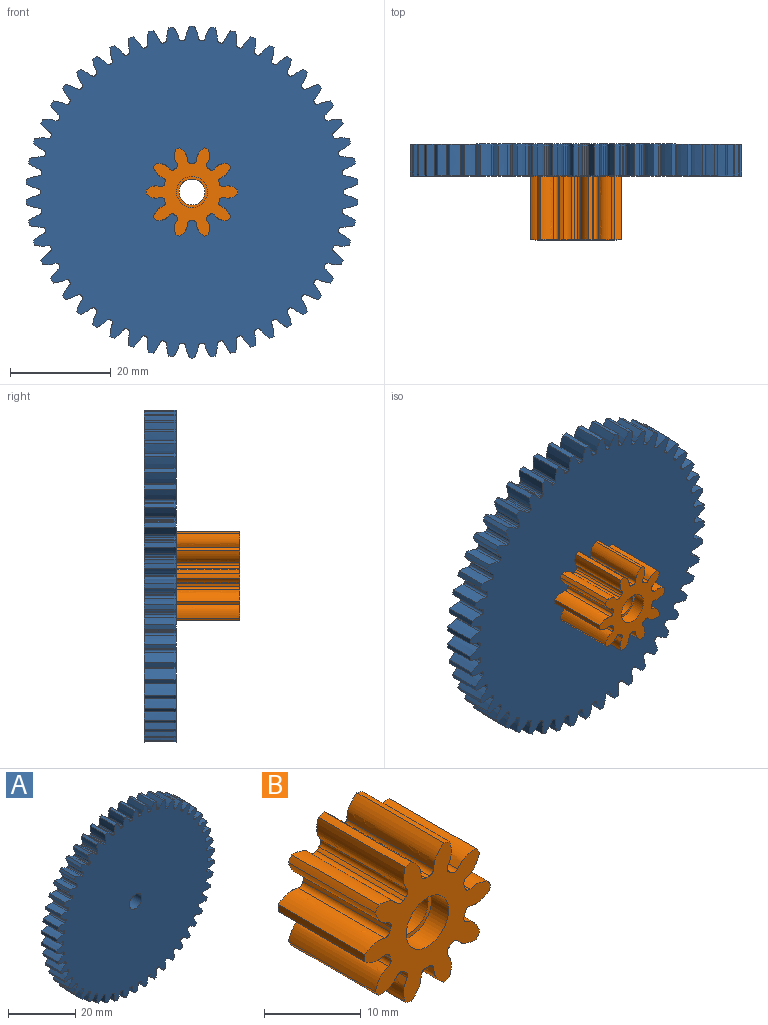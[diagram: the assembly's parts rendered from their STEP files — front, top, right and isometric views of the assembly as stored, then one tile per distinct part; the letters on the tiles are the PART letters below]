
ASSEMBLY  parts=2 mates=1
PART A: 305 faces, bbox 66x6.4x66 mm
  f0: cylinder r=2.59mm len=5.18mm, axis (0,-1,0), area 62.7mm2, adj f50,f303
  f1: cylinder r=33.02mm len=6.35mm, axis (0,1,0), area 6.2mm2, adj f50,f52,f53,f300
  f2: cylinder r=33.02mm len=6.35mm, axis (0,1,0), area 6.2mm2, adj f50,f52,f295,f298
  f3: cylinder r=33.02mm len=6.35mm, axis (0,1,0), area 6.2mm2, adj f50,f52,f290,f293
  f4: cylinder r=33.02mm len=6.35mm, axis (0,1,0), area 6.2mm2, adj f50,f52,f285,f288
  f5: cylinder r=33.02mm len=6.35mm, axis (0,1,0), area 6.2mm2, adj f50,f52,f263,f280
  f6: cylinder r=33.02mm len=6.35mm, axis (0,1,0), area 6.2mm2, adj f50,f52,f275,f278
  f7: cylinder r=33.02mm len=6.35mm, axis (0,1,0), area 6.2mm2, adj f50,f52,f270,f283
  f8: cylinder r=33.02mm len=6.35mm, axis (0,1,0), area 6.2mm2, adj f50,f52,f265,f268
  f9: cylinder r=33.02mm len=6.35mm, axis (0,1,0), area 6.2mm2, adj f50,f52,f260,f273
  f10: cylinder r=33.02mm len=6.35mm, axis (0,1,0), area 6.2mm2, adj f50,f52,f255,f258
  f11: cylinder r=33.02mm len=6.35mm, axis (0,1,0), area 6.2mm2, adj f50,f52,f250,f253
  f12: cylinder r=33.02mm len=6.35mm, axis (0,1,0), area 6.2mm2, adj f50,f52,f245,f248
  f13: cylinder r=33.02mm len=6.35mm, axis (0,1,0), area 6.2mm2, adj f50,f52,f240,f243
  f14: cylinder r=33.02mm len=6.35mm, axis (0,1,0), area 6.2mm2, adj f50,f52,f235,f238
  f15: cylinder r=33.02mm len=6.35mm, axis (0,1,0), area 6.2mm2, adj f50,f52,f230,f233
  f16: cylinder r=33.02mm len=6.35mm, axis (0,1,0), area 6.2mm2, adj f50,f52,f225,f228
  f17: cylinder r=33.02mm len=6.35mm, axis (0,1,0), area 6.2mm2, adj f50,f52,f203,f220
  f18: cylinder r=33.02mm len=6.35mm, axis (0,1,0), area 6.2mm2, adj f50,f52,f215,f218
  f19: cylinder r=33.02mm len=6.35mm, axis (0,1,0), area 6.2mm2, adj f50,f52,f210,f223
  f20: cylinder r=33.02mm len=6.35mm, axis (0,1,0), area 6.2mm2, adj f50,f52,f205,f208
  f21: cylinder r=33.02mm len=6.35mm, axis (0,1,0), area 6.2mm2, adj f50,f52,f200,f213
  f22: cylinder r=33.02mm len=6.35mm, axis (0,1,0), area 6.2mm2, adj f50,f52,f195,f198
  f23: cylinder r=33.02mm len=6.35mm, axis (0,1,0), area 6.2mm2, adj f50,f52,f190,f193
  f24: cylinder r=33.02mm len=6.35mm, axis (0,1,0), area 6.2mm2, adj f50,f52,f185,f188
  f25: cylinder r=33.02mm len=6.35mm, axis (0,1,0), area 6.2mm2, adj f50,f52,f180,f183
  f26: cylinder r=33.02mm len=6.35mm, axis (0,1,0), area 6.2mm2, adj f50,f52,f175,f178
  f27: cylinder r=33.02mm len=6.35mm, axis (0,1,0), area 6.2mm2, adj f50,f52,f170,f173
  f28: cylinder r=33.02mm len=6.35mm, axis (0,1,0), area 6.2mm2, adj f50,f52,f165,f168
  f29: cylinder r=33.02mm len=6.35mm, axis (0,1,0), area 6.2mm2, adj f50,f52,f148,f160
  f30: cylinder r=33.02mm len=6.35mm, axis (0,1,0), area 6.2mm2, adj f50,f52,f155,f158
  f31: cylinder r=33.02mm len=6.35mm, axis (0,1,0), area 6.2mm2, adj f50,f52,f143,f150
  f32: cylinder r=33.02mm len=6.35mm, axis (0,1,0), area 6.2mm2, adj f50,f52,f145,f163
  f33: cylinder r=33.02mm len=6.35mm, axis (0,1,0), area 6.2mm2, adj f50,f52,f140,f153
  f34: cylinder r=33.02mm len=6.35mm, axis (0,1,0), area 6.2mm2, adj f50,f52,f135,f138
  f35: cylinder r=33.02mm len=6.35mm, axis (0,1,0), area 6.2mm2, adj f50,f52,f130,f133
  f36: cylinder r=33.02mm len=6.35mm, axis (0,1,0), area 6.2mm2, adj f50,f52,f125,f128
  f37: cylinder r=33.02mm len=6.35mm, axis (0,1,0), area 6.2mm2, adj f50,f52,f120,f123
  f38: cylinder r=33.02mm len=6.35mm, axis (0,1,0), area 6.2mm2, adj f50,f52,f115,f118
  f39: cylinder r=33.02mm len=6.35mm, axis (0,1,0), area 6.2mm2, adj f50,f52,f110,f113
  f40: cylinder r=33.02mm len=6.35mm, axis (0,1,0), area 6.2mm2, adj f50,f52,f105,f108
  f41: cylinder r=33.02mm len=6.35mm, axis (0,1,0), area 6.2mm2, adj f50,f52,f93,f100
  f42: cylinder r=33.02mm len=6.35mm, axis (0,1,0), area 6.2mm2, adj f50,f52,f88,f95
  f43: cylinder r=33.02mm len=6.35mm, axis (0,1,0), area 6.2mm2, adj f50,f52,f83,f90
  f44: cylinder r=33.02mm len=6.35mm, axis (0,1,0), area 6.2mm2, adj f50,f52,f68,f85
  f45: cylinder r=33.02mm len=6.35mm, axis (0,1,0), area 6.2mm2, adj f50,f52,f80,f103
  f46: cylinder r=33.02mm len=6.35mm, axis (0,1,0), area 6.2mm2, adj f50,f52,f75,f78
  f47: cylinder r=33.02mm len=6.35mm, axis (0,1,0), area 6.2mm2, adj f50,f52,f63,f70
  f48: cylinder r=33.02mm len=6.35mm, axis (0,1,0), area 6.2mm2, adj f50,f52,f65,f73
  f49: cylinder r=33.02mm len=6.35mm, axis (0,1,0), area 6.2mm2, adj f50,f52,f60,f98
  f50: plane 66.04x65.97mm, normal (0,-1,0), area 3128.1mm2, adj f0,f1,f2,f3,f4,f5,f6,f7
  f51: cylinder r=33.02mm len=6.35mm, axis (0,1,0), area 6.2mm2, adj f50,f52,f55,f58
  f52: plane 66.04x65.97mm, normal (0,1,0), area 3119mm2, adj f1,f2,f3,f4,f5,f6,f7,f8
  f53: extruded ~6.35x2.48mm, area 17mm2, adj f1,f50,f52,f56
  f54: cylinder r=30.16mm len=6.35mm, axis (0,1,0), area 2.2mm2, adj f50,f52,f56,f57
  f55: extruded ~6.35x2.48mm, area 17mm2, adj f50,f51,f52,f57
  f56: cylinder r=0.44mm len=6.35mm, axis (0,1,0), area 3.8mm2, adj f50,f52,f53,f54
  f57: cylinder r=0.44mm len=6.35mm, axis (0,1,0), area 3.8mm2, adj f50,f52,f54,f55
  f58: extruded ~6.35x2.58mm, area 17mm2, adj f50,f51,f52,f61
  f59: cylinder r=30.16mm len=6.35mm, axis (0,1,0), area 2.2mm2, adj f50,f52,f61,f62
  f60: extruded ~6.35x2.34mm, area 17mm2, adj f49,f50,f52,f62
  f61: cylinder r=0.44mm len=6.35mm, axis (0,1,0), area 3.8mm2, adj f50,f52,f58,f59
  f62: cylinder r=0.44mm len=6.35mm, axis (0,1,0), area 3.8mm2, adj f50,f52,f59,f60
  f63: extruded ~6.35x2.34mm, area 17mm2, adj f47,f50,f52,f66
  f64: cylinder r=30.16mm len=6.35mm, axis (0,1,0), area 2.2mm2, adj f50,f52,f66,f67
  f65: extruded ~6.35x2.54mm, area 17mm2, adj f48,f50,f52,f67
  f66: cylinder r=0.44mm len=6.35mm, axis (0,1,0), area 3.8mm2, adj f50,f52,f63,f64
  f67: cylinder r=0.44mm len=6.35mm, axis (0,1,0), area 3.8mm2, adj f50,f52,f64,f65
  f68: extruded ~6.35x2.48mm, area 17mm2, adj f44,f50,f52,f71
  f69: cylinder r=30.16mm len=6.35mm, axis (0,1,0), area 2.2mm2, adj f50,f52,f71,f72
  f70: extruded ~6.35x2.42mm, area 17mm2, adj f47,f50,f52,f72
  f71: cylinder r=0.44mm len=6.35mm, axis (0,1,0), area 3.8mm2, adj f50,f52,f68,f69
  f72: cylinder r=0.44mm len=6.35mm, axis (0,1,0), area 3.8mm2, adj f50,f52,f69,f70
  f73: extruded ~6.35x2.16mm, area 17mm2, adj f48,f50,f52,f76
  f74: cylinder r=30.16mm len=6.35mm, axis (0,1,0), area 2.2mm2, adj f50,f52,f76,f77
  f75: extruded ~6.35x2.62mm, area 17mm2, adj f46,f50,f52,f77
  f76: cylinder r=0.44mm len=6.35mm, axis (0,1,0), area 3.8mm2, adj f50,f52,f73,f74
  f77: cylinder r=0.44mm len=6.35mm, axis (0,1,0), area 3.8mm2, adj f50,f52,f74,f75
  f78: extruded ~6.35x1.95mm, area 17mm2, adj f46,f50,f52,f81
  f79: cylinder r=30.16mm len=6.35mm, axis (0,1,0), area 2.2mm2, adj f50,f52,f81,f82
  f80: extruded ~6.35x2.66mm, area 17mm2, adj f45,f50,f52,f82
  f81: cylinder r=0.44mm len=6.35mm, axis (0,1,0), area 3.8mm2, adj f50,f52,f78,f79
  f82: cylinder r=0.44mm len=6.35mm, axis (0,1,0), area 3.8mm2, adj f50,f52,f79,f80
  f83: extruded ~6.35x2.59mm, area 17mm2, adj f43,f50,f52,f86
  f84: cylinder r=30.16mm len=6.35mm, axis (0,1,0), area 2.2mm2, adj f50,f52,f86,f87
  f85: extruded ~6.35x2.25mm, area 17mm2, adj f44,f50,f52,f87
  f86: cylinder r=0.44mm len=6.35mm, axis (0,1,0), area 3.8mm2, adj f50,f52,f83,f84
  f87: cylinder r=0.44mm len=6.35mm, axis (0,1,0), area 3.8mm2, adj f50,f52,f84,f85
  f88: extruded ~6.35x2.65mm, area 17mm2, adj f42,f50,f52,f91
  f89: cylinder r=30.16mm len=6.35mm, axis (0,1,0), area 2.2mm2, adj f50,f52,f91,f92
  f90: extruded ~6.35x2.06mm, area 17mm2, adj f43,f50,f52,f92
  f91: cylinder r=0.44mm len=6.35mm, axis (0,1,0), area 3.8mm2, adj f50,f52,f88,f89
  f92: cylinder r=0.44mm len=6.35mm, axis (0,1,0), area 3.8mm2, adj f50,f52,f89,f90
  f93: extruded ~6.35x2.67mm, area 17mm2, adj f41,f50,f52,f96
  f94: cylinder r=30.16mm len=6.35mm, axis (0,1,0), area 2.2mm2, adj f50,f52,f96,f97
  f95: extruded ~6.35x1.94mm, area 17mm2, adj f42,f50,f52,f97
  f96: cylinder r=0.44mm len=6.35mm, axis (0,1,0), area 3.8mm2, adj f50,f52,f93,f94
  f97: cylinder r=0.44mm len=6.35mm, axis (0,1,0), area 3.8mm2, adj f50,f52,f94,f95
  f98: extruded ~6.35x2.65mm, area 17mm2, adj f49,f50,f52,f101
  f99: cylinder r=30.16mm len=6.35mm, axis (0,1,0), area 2.2mm2, adj f50,f52,f101,f102
  f100: extruded ~6.35x2.16mm, area 17mm2, adj f41,f50,f52,f102
  f101: cylinder r=0.44mm len=6.35mm, axis (0,1,0), area 3.8mm2, adj f50,f52,f98,f99
  f102: cylinder r=0.44mm len=6.35mm, axis (0,1,0), area 3.8mm2, adj f50,f52,f99,f100
  f103: extruded ~6.35x2.06mm, area 17mm2, adj f45,f50,f52,f106
  f104: cylinder r=30.16mm len=6.35mm, axis (0,1,0), area 2.2mm2, adj f50,f52,f106,f107
  f105: extruded ~6.35x2.66mm, area 17mm2, adj f40,f50,f52,f107
  f106: cylinder r=0.44mm len=6.35mm, axis (0,1,0), area 3.8mm2, adj f50,f52,f103,f104
  f107: cylinder r=0.44mm len=6.35mm, axis (0,1,0), area 3.8mm2, adj f50,f52,f104,f105
  f108: extruded ~6.35x2.25mm, area 17mm2, adj f40,f50,f52,f111
  f109: cylinder r=30.16mm len=6.35mm, axis (0,1,0), area 2.2mm2, adj f50,f52,f111,f112
  f110: extruded ~6.35x2.62mm, area 17mm2, adj f39,f50,f52,f112
  f111: cylinder r=0.44mm len=6.35mm, axis (0,1,0), area 3.8mm2, adj f50,f52,f108,f109
  f112: cylinder r=0.44mm len=6.35mm, axis (0,1,0), area 3.8mm2, adj f50,f52,f109,f110
  f113: extruded ~6.35x2.41mm, area 17mm2, adj f39,f50,f52,f116
  f114: cylinder r=30.16mm len=6.35mm, axis (0,1,0), area 2.2mm2, adj f50,f52,f116,f117
  f115: extruded ~6.35x2.54mm, area 17mm2, adj f38,f50,f52,f117
  f116: cylinder r=0.44mm len=6.35mm, axis (0,1,0), area 3.8mm2, adj f50,f52,f113,f114
  f117: cylinder r=0.44mm len=6.35mm, axis (0,1,0), area 3.8mm2, adj f50,f52,f114,f115
  f118: extruded ~6.35x2.54mm, area 17mm2, adj f38,f50,f52,f121
  f119: cylinder r=30.16mm len=6.35mm, axis (0,1,0), area 2.2mm2, adj f50,f52,f121,f122
  f120: extruded ~6.35x2.41mm, area 17mm2, adj f37,f50,f52,f122
  f121: cylinder r=0.44mm len=6.35mm, axis (0,1,0), area 3.8mm2, adj f50,f52,f118,f119
  f122: cylinder r=0.44mm len=6.35mm, axis (0,1,0), area 3.8mm2, adj f50,f52,f119,f120
  f123: extruded ~6.35x2.62mm, area 17mm2, adj f37,f50,f52,f126
  f124: cylinder r=30.16mm len=6.35mm, axis (0,1,0), area 2.2mm2, adj f50,f52,f126,f127
  f125: extruded ~6.35x2.25mm, area 17mm2, adj f36,f50,f52,f127
  f126: cylinder r=0.44mm len=6.35mm, axis (0,1,0), area 3.8mm2, adj f50,f52,f123,f124
  f127: cylinder r=0.44mm len=6.35mm, axis (0,1,0), area 3.8mm2, adj f50,f52,f124,f125
  f128: extruded ~6.35x2.66mm, area 17mm2, adj f36,f50,f52,f131
  f129: cylinder r=30.16mm len=6.35mm, axis (0,1,0), area 2.2mm2, adj f50,f52,f131,f132
  f130: extruded ~6.35x2.06mm, area 17mm2, adj f35,f50,f52,f132
  f131: cylinder r=0.44mm len=6.35mm, axis (0,1,0), area 3.8mm2, adj f50,f52,f128,f129
  f132: cylinder r=0.44mm len=6.35mm, axis (0,1,0), area 3.8mm2, adj f50,f52,f129,f130
  f133: extruded ~6.35x2.66mm, area 17mm2, adj f35,f50,f52,f136
  f134: cylinder r=30.16mm len=6.35mm, axis (0,1,0), area 2.2mm2, adj f50,f52,f136,f137
  f135: extruded ~6.35x1.95mm, area 17mm2, adj f34,f50,f52,f137
  f136: cylinder r=0.44mm len=6.35mm, axis (0,1,0), area 3.8mm2, adj f50,f52,f133,f134
  f137: cylinder r=0.44mm len=6.35mm, axis (0,1,0), area 3.8mm2, adj f50,f52,f134,f135
  f138: extruded ~6.35x2.62mm, area 17mm2, adj f34,f50,f52,f141
  f139: cylinder r=30.16mm len=6.35mm, axis (0,1,0), area 2.2mm2, adj f50,f52,f141,f142
  f140: extruded ~6.35x2.16mm, area 17mm2, adj f33,f50,f52,f142
  f141: cylinder r=0.44mm len=6.35mm, axis (0,1,0), area 3.8mm2, adj f50,f52,f138,f139
  f142: cylinder r=0.44mm len=6.35mm, axis (0,1,0), area 3.8mm2, adj f50,f52,f139,f140
  f143: extruded ~6.35x2.06mm, area 17mm2, adj f31,f50,f52,f146
  f144: cylinder r=30.16mm len=6.35mm, axis (0,1,0), area 2.2mm2, adj f50,f52,f146,f147
  f145: extruded ~6.35x2.65mm, area 17mm2, adj f32,f50,f52,f147
  f146: cylinder r=0.44mm len=6.35mm, axis (0,1,0), area 3.8mm2, adj f50,f52,f143,f144
  f147: cylinder r=0.44mm len=6.35mm, axis (0,1,0), area 3.8mm2, adj f50,f52,f144,f145
  f148: extruded ~6.35x2.25mm, area 17mm2, adj f29,f50,f52,f151
  f149: cylinder r=30.16mm len=6.35mm, axis (0,1,0), area 2.2mm2, adj f50,f52,f151,f152
  f150: extruded ~6.35x2.59mm, area 17mm2, adj f31,f50,f52,f152
  f151: cylinder r=0.44mm len=6.35mm, axis (0,1,0), area 3.8mm2, adj f50,f52,f148,f149
  f152: cylinder r=0.44mm len=6.35mm, axis (0,1,0), area 3.8mm2, adj f50,f52,f149,f150
  f153: extruded ~6.35x2.54mm, area 17mm2, adj f33,f50,f52,f156
  f154: cylinder r=30.16mm len=6.35mm, axis (0,1,0), area 2.2mm2, adj f50,f52,f156,f157
  f155: extruded ~6.35x2.34mm, area 17mm2, adj f30,f50,f52,f157
  f156: cylinder r=0.44mm len=6.35mm, axis (0,1,0), area 3.8mm2, adj f50,f52,f153,f154
  f157: cylinder r=0.44mm len=6.35mm, axis (0,1,0), area 3.8mm2, adj f50,f52,f154,f155
  f158: extruded ~6.35x2.42mm, area 17mm2, adj f30,f50,f52,f161
  f159: cylinder r=30.16mm len=6.35mm, axis (0,1,0), area 2.2mm2, adj f50,f52,f161,f162
  f160: extruded ~6.35x2.48mm, area 17mm2, adj f29,f50,f52,f162
  f161: cylinder r=0.44mm len=6.35mm, axis (0,1,0), area 3.8mm2, adj f50,f52,f158,f159
  f162: cylinder r=0.44mm len=6.35mm, axis (0,1,0), area 3.8mm2, adj f50,f52,f159,f160
  f163: extruded ~6.35x1.94mm, area 17mm2, adj f32,f50,f52,f166
  f164: cylinder r=30.16mm len=6.35mm, axis (0,1,0), area 2.2mm2, adj f50,f52,f166,f167
  f165: extruded ~6.35x2.67mm, area 17mm2, adj f28,f50,f52,f167
  f166: cylinder r=0.44mm len=6.35mm, axis (0,1,0), area 3.8mm2, adj f50,f52,f163,f164
  f167: cylinder r=0.44mm len=6.35mm, axis (0,1,0), area 3.8mm2, adj f50,f52,f164,f165
  f168: extruded ~6.35x2.16mm, area 17mm2, adj f28,f50,f52,f171
  f169: cylinder r=30.16mm len=6.35mm, axis (0,1,0), area 2.2mm2, adj f50,f52,f171,f172
  f170: extruded ~6.35x2.65mm, area 17mm2, adj f27,f50,f52,f172
  f171: cylinder r=0.44mm len=6.35mm, axis (0,1,0), area 3.8mm2, adj f50,f52,f168,f169
  f172: cylinder r=0.44mm len=6.35mm, axis (0,1,0), area 3.8mm2, adj f50,f52,f169,f170
  f173: extruded ~6.35x2.34mm, area 17mm2, adj f27,f50,f52,f176
  f174: cylinder r=30.16mm len=6.35mm, axis (0,1,0), area 2.2mm2, adj f50,f52,f176,f177
  f175: extruded ~6.35x2.58mm, area 17mm2, adj f26,f50,f52,f177
  f176: cylinder r=0.44mm len=6.35mm, axis (0,1,0), area 3.8mm2, adj f50,f52,f173,f174
  f177: cylinder r=0.44mm len=6.35mm, axis (0,1,0), area 3.8mm2, adj f50,f52,f174,f175
  f178: extruded ~6.35x2.48mm, area 17mm2, adj f26,f50,f52,f181
  f179: cylinder r=30.16mm len=6.35mm, axis (0,1,0), area 2.2mm2, adj f50,f52,f181,f182
  f180: extruded ~6.35x2.48mm, area 17mm2, adj f25,f50,f52,f182
  f181: cylinder r=0.44mm len=6.35mm, axis (0,1,0), area 3.8mm2, adj f50,f52,f178,f179
  f182: cylinder r=0.44mm len=6.35mm, axis (0,1,0), area 3.8mm2, adj f50,f52,f179,f180
  f183: extruded ~6.35x2.58mm, area 17mm2, adj f25,f50,f52,f186
  f184: cylinder r=30.16mm len=6.35mm, axis (0,1,0), area 2.2mm2, adj f50,f52,f186,f187
  f185: extruded ~6.35x2.34mm, area 17mm2, adj f24,f50,f52,f187
  f186: cylinder r=0.44mm len=6.35mm, axis (0,1,0), area 3.8mm2, adj f50,f52,f183,f184
  f187: cylinder r=0.44mm len=6.35mm, axis (0,1,0), area 3.8mm2, adj f50,f52,f184,f185
  f188: extruded ~6.35x2.65mm, area 17mm2, adj f24,f50,f52,f191
  f189: cylinder r=30.16mm len=6.35mm, axis (0,1,0), area 2.2mm2, adj f50,f52,f191,f192
  f190: extruded ~6.35x2.16mm, area 17mm2, adj f23,f50,f52,f192
  f191: cylinder r=0.44mm len=6.35mm, axis (0,1,0), area 3.8mm2, adj f50,f52,f188,f189
  f192: cylinder r=0.44mm len=6.35mm, axis (0,1,0), area 3.8mm2, adj f50,f52,f189,f190
  f193: extruded ~6.35x2.67mm, area 17mm2, adj f23,f50,f52,f196
  f194: cylinder r=30.16mm len=6.35mm, axis (0,1,0), area 2.2mm2, adj f50,f52,f196,f197
  f195: extruded ~6.35x1.94mm, area 17mm2, adj f22,f50,f52,f197
  f196: cylinder r=0.44mm len=6.35mm, axis (0,1,0), area 3.8mm2, adj f50,f52,f193,f194
  f197: cylinder r=0.44mm len=6.35mm, axis (0,1,0), area 3.8mm2, adj f50,f52,f194,f195
  f198: extruded ~6.35x2.65mm, area 17mm2, adj f22,f50,f52,f201
  f199: cylinder r=30.16mm len=6.35mm, axis (0,1,0), area 2.2mm2, adj f50,f52,f201,f202
  f200: extruded ~6.35x2.06mm, area 17mm2, adj f21,f50,f52,f202
  f201: cylinder r=0.44mm len=6.35mm, axis (0,1,0), area 3.8mm2, adj f50,f52,f198,f199
  f202: cylinder r=0.44mm len=6.35mm, axis (0,1,0), area 3.8mm2, adj f50,f52,f199,f200
  f203: extruded ~6.35x2.34mm, area 17mm2, adj f17,f50,f52,f206
  f204: cylinder r=30.16mm len=6.35mm, axis (0,1,0), area 2.2mm2, adj f50,f52,f206,f207
  f205: extruded ~6.35x2.54mm, area 17mm2, adj f20,f50,f52,f207
  f206: cylinder r=0.44mm len=6.35mm, axis (0,1,0), area 3.8mm2, adj f50,f52,f203,f204
  f207: cylinder r=0.44mm len=6.35mm, axis (0,1,0), area 3.8mm2, adj f50,f52,f204,f205
  f208: extruded ~6.35x2.16mm, area 17mm2, adj f20,f50,f52,f211
  f209: cylinder r=30.16mm len=6.35mm, axis (0,1,0), area 2.2mm2, adj f50,f52,f211,f212
  f210: extruded ~6.35x2.62mm, area 17mm2, adj f19,f50,f52,f212
  f211: cylinder r=0.44mm len=6.35mm, axis (0,1,0), area 3.8mm2, adj f50,f52,f208,f209
  f212: cylinder r=0.44mm len=6.35mm, axis (0,1,0), area 3.8mm2, adj f50,f52,f209,f210
  f213: extruded ~6.35x2.59mm, area 17mm2, adj f21,f50,f52,f216
  f214: cylinder r=30.16mm len=6.35mm, axis (0,1,0), area 2.2mm2, adj f50,f52,f216,f217
  f215: extruded ~6.35x2.25mm, area 17mm2, adj f18,f50,f52,f217
  f216: cylinder r=0.44mm len=6.35mm, axis (0,1,0), area 3.8mm2, adj f50,f52,f213,f214
  f217: cylinder r=0.44mm len=6.35mm, axis (0,1,0), area 3.8mm2, adj f50,f52,f214,f215
  f218: extruded ~6.35x2.48mm, area 17mm2, adj f18,f50,f52,f221
  f219: cylinder r=30.16mm len=6.35mm, axis (0,1,0), area 2.2mm2, adj f50,f52,f221,f222
  f220: extruded ~6.35x2.42mm, area 17mm2, adj f17,f50,f52,f222
  f221: cylinder r=0.44mm len=6.35mm, axis (0,1,0), area 3.8mm2, adj f50,f52,f218,f219
  f222: cylinder r=0.44mm len=6.35mm, axis (0,1,0), area 3.8mm2, adj f50,f52,f219,f220
  f223: extruded ~6.35x1.95mm, area 17mm2, adj f19,f50,f52,f226
  f224: cylinder r=30.16mm len=6.35mm, axis (0,1,0), area 2.2mm2, adj f50,f52,f226,f227
  f225: extruded ~6.35x2.66mm, area 17mm2, adj f16,f50,f52,f227
  f226: cylinder r=0.44mm len=6.35mm, axis (0,1,0), area 3.8mm2, adj f50,f52,f223,f224
  f227: cylinder r=0.44mm len=6.35mm, axis (0,1,0), area 3.8mm2, adj f50,f52,f224,f225
  f228: extruded ~6.35x2.06mm, area 17mm2, adj f16,f50,f52,f231
  f229: cylinder r=30.16mm len=6.35mm, axis (0,1,0), area 2.2mm2, adj f50,f52,f231,f232
  f230: extruded ~6.35x2.66mm, area 17mm2, adj f15,f50,f52,f232
  f231: cylinder r=0.44mm len=6.35mm, axis (0,1,0), area 3.8mm2, adj f50,f52,f228,f229
  f232: cylinder r=0.44mm len=6.35mm, axis (0,1,0), area 3.8mm2, adj f50,f52,f229,f230
  f233: extruded ~6.35x2.25mm, area 17mm2, adj f15,f50,f52,f236
  f234: cylinder r=30.16mm len=6.35mm, axis (0,1,0), area 2.2mm2, adj f50,f52,f236,f237
  f235: extruded ~6.35x2.62mm, area 17mm2, adj f14,f50,f52,f237
  f236: cylinder r=0.44mm len=6.35mm, axis (0,1,0), area 3.8mm2, adj f50,f52,f233,f234
  f237: cylinder r=0.44mm len=6.35mm, axis (0,1,0), area 3.8mm2, adj f50,f52,f234,f235
  f238: extruded ~6.35x2.41mm, area 17mm2, adj f14,f50,f52,f241
  f239: cylinder r=30.16mm len=6.35mm, axis (0,1,0), area 2.2mm2, adj f50,f52,f241,f242
  f240: extruded ~6.35x2.54mm, area 17mm2, adj f13,f50,f52,f242
  f241: cylinder r=0.44mm len=6.35mm, axis (0,1,0), area 3.8mm2, adj f50,f52,f238,f239
  f242: cylinder r=0.44mm len=6.35mm, axis (0,1,0), area 3.8mm2, adj f50,f52,f239,f240
  f243: extruded ~6.35x2.54mm, area 17mm2, adj f13,f50,f52,f246
  f244: cylinder r=30.16mm len=6.35mm, axis (0,1,0), area 2.2mm2, adj f50,f52,f246,f247
  f245: extruded ~6.35x2.41mm, area 17mm2, adj f12,f50,f52,f247
  f246: cylinder r=0.44mm len=6.35mm, axis (0,1,0), area 3.8mm2, adj f50,f52,f243,f244
  f247: cylinder r=0.44mm len=6.35mm, axis (0,1,0), area 3.8mm2, adj f50,f52,f244,f245
  f248: extruded ~6.35x2.62mm, area 17mm2, adj f12,f50,f52,f251
  f249: cylinder r=30.16mm len=6.35mm, axis (0,1,0), area 2.2mm2, adj f50,f52,f251,f252
  f250: extruded ~6.35x2.25mm, area 17mm2, adj f11,f50,f52,f252
  f251: cylinder r=0.44mm len=6.35mm, axis (0,1,0), area 3.8mm2, adj f50,f52,f248,f249
  f252: cylinder r=0.44mm len=6.35mm, axis (0,1,0), area 3.8mm2, adj f50,f52,f249,f250
  f253: extruded ~6.35x2.66mm, area 17mm2, adj f11,f50,f52,f256
  f254: cylinder r=30.16mm len=6.35mm, axis (0,1,0), area 2.2mm2, adj f50,f52,f256,f257
  f255: extruded ~6.35x2.06mm, area 17mm2, adj f10,f50,f52,f257
  f256: cylinder r=0.44mm len=6.35mm, axis (0,1,0), area 3.8mm2, adj f50,f52,f253,f254
  f257: cylinder r=0.44mm len=6.35mm, axis (0,1,0), area 3.8mm2, adj f50,f52,f254,f255
  f258: extruded ~6.35x2.66mm, area 17mm2, adj f10,f50,f52,f261
  f259: cylinder r=30.16mm len=6.35mm, axis (0,1,0), area 2.2mm2, adj f50,f52,f261,f262
  f260: extruded ~6.35x1.95mm, area 17mm2, adj f9,f50,f52,f262
  f261: cylinder r=0.44mm len=6.35mm, axis (0,1,0), area 3.8mm2, adj f50,f52,f258,f259
  f262: cylinder r=0.44mm len=6.35mm, axis (0,1,0), area 3.8mm2, adj f50,f52,f259,f260
  f263: extruded ~6.35x2.42mm, area 17mm2, adj f5,f50,f52,f266
  f264: cylinder r=30.16mm len=6.35mm, axis (0,1,0), area 2.2mm2, adj f50,f52,f266,f267
  f265: extruded ~6.35x2.48mm, area 17mm2, adj f8,f50,f52,f267
  f266: cylinder r=0.44mm len=6.35mm, axis (0,1,0), area 3.8mm2, adj f50,f52,f263,f264
  f267: cylinder r=0.44mm len=6.35mm, axis (0,1,0), area 3.8mm2, adj f50,f52,f264,f265
  f268: extruded ~6.35x2.25mm, area 17mm2, adj f8,f50,f52,f271
  f269: cylinder r=30.16mm len=6.35mm, axis (0,1,0), area 2.2mm2, adj f50,f52,f271,f272
  f270: extruded ~6.35x2.59mm, area 17mm2, adj f7,f50,f52,f272
  f271: cylinder r=0.44mm len=6.35mm, axis (0,1,0), area 3.8mm2, adj f50,f52,f268,f269
  f272: cylinder r=0.44mm len=6.35mm, axis (0,1,0), area 3.8mm2, adj f50,f52,f269,f270
  f273: extruded ~6.35x2.62mm, area 17mm2, adj f9,f50,f52,f276
  f274: cylinder r=30.16mm len=6.35mm, axis (0,1,0), area 2.2mm2, adj f50,f52,f276,f277
  f275: extruded ~6.35x2.16mm, area 17mm2, adj f6,f50,f52,f277
  f276: cylinder r=0.44mm len=6.35mm, axis (0,1,0), area 3.8mm2, adj f50,f52,f273,f274
  f277: cylinder r=0.44mm len=6.35mm, axis (0,1,0), area 3.8mm2, adj f50,f52,f274,f275
  f278: extruded ~6.35x2.54mm, area 17mm2, adj f6,f50,f52,f281
  f279: cylinder r=30.16mm len=6.35mm, axis (0,1,0), area 2.2mm2, adj f50,f52,f281,f282
  f280: extruded ~6.35x2.34mm, area 17mm2, adj f5,f50,f52,f282
  f281: cylinder r=0.44mm len=6.35mm, axis (0,1,0), area 3.8mm2, adj f50,f52,f278,f279
  f282: cylinder r=0.44mm len=6.35mm, axis (0,1,0), area 3.8mm2, adj f50,f52,f279,f280
  f283: extruded ~6.35x2.06mm, area 17mm2, adj f7,f50,f52,f286
  f284: cylinder r=30.16mm len=6.35mm, axis (0,1,0), area 2.2mm2, adj f50,f52,f286,f287
  f285: extruded ~6.35x2.65mm, area 17mm2, adj f4,f50,f52,f287
  f286: cylinder r=0.44mm len=6.35mm, axis (0,1,0), area 3.8mm2, adj f50,f52,f283,f284
  f287: cylinder r=0.44mm len=6.35mm, axis (0,1,0), area 3.8mm2, adj f50,f52,f284,f285
  f288: extruded ~6.35x1.94mm, area 17mm2, adj f4,f50,f52,f291
  f289: cylinder r=30.16mm len=6.35mm, axis (0,1,0), area 2.2mm2, adj f50,f52,f291,f292
  f290: extruded ~6.35x2.67mm, area 17mm2, adj f3,f50,f52,f292
  f291: cylinder r=0.44mm len=6.35mm, axis (0,1,0), area 3.8mm2, adj f50,f52,f288,f289
  f292: cylinder r=0.44mm len=6.35mm, axis (0,1,0), area 3.8mm2, adj f50,f52,f289,f290
  f293: extruded ~6.35x2.16mm, area 17mm2, adj f3,f50,f52,f296
  f294: cylinder r=30.16mm len=6.35mm, axis (0,1,0), area 2.2mm2, adj f50,f52,f296,f297
  f295: extruded ~6.35x2.65mm, area 17mm2, adj f2,f50,f52,f297
  f296: cylinder r=0.44mm len=6.35mm, axis (0,1,0), area 3.8mm2, adj f50,f52,f293,f294
  f297: cylinder r=0.44mm len=6.35mm, axis (0,1,0), area 3.8mm2, adj f50,f52,f294,f295
  f298: extruded ~6.35x2.34mm, area 17mm2, adj f2,f50,f52,f301
  f299: cylinder r=30.16mm len=6.35mm, axis (0,1,0), area 2.2mm2, adj f50,f52,f301,f302
  f300: extruded ~6.35x2.58mm, area 17mm2, adj f1,f50,f52,f302
  f301: cylinder r=0.44mm len=6.35mm, axis (0,1,0), area 3.8mm2, adj f50,f52,f298,f299
  f302: cylinder r=0.44mm len=6.35mm, axis (0,1,0), area 3.8mm2, adj f50,f52,f299,f300
  f303: plane 6.2x6.2mm, normal (0,1,0), area 9.1mm2, adj f0,f304
  f304: cylinder r=3.1mm len=6.2mm, axis (0,1,0), area 48.7mm2, adj f52,f303
PART B: 65 faces, bbox 18.3x12.7x17.7 mm
  f0: cylinder r=2.58mm len=10.2mm, axis (0,-1,0), area 165.6mm2, adj f12,f63
  f1: cylinder r=9.14mm len=12.7mm, axis (0,1,0), area 11.4mm2, adj f10,f12,f15,f59
  f2: cylinder r=9.14mm len=12.7mm, axis (0,1,0), area 11.4mm2, adj f10,f12,f54,f60
  f3: cylinder r=9.14mm len=12.7mm, axis (0,1,0), area 11.4mm2, adj f10,f12,f45,f49
  f4: cylinder r=9.14mm len=12.7mm, axis (0,1,0), area 11.4mm2, adj f10,f12,f44,f55
  f5: cylinder r=9.14mm len=12.7mm, axis (0,1,0), area 11.4mm2, adj f10,f12,f35,f39
  f6: cylinder r=9.14mm len=12.7mm, axis (0,1,0), area 11.4mm2, adj f10,f12,f34,f50
  f7: cylinder r=9.14mm len=12.7mm, axis (0,1,0), area 11.4mm2, adj f10,f12,f29,f40
  f8: cylinder r=9.14mm len=12.7mm, axis (0,1,0), area 11.4mm2, adj f10,f12,f24,f30
  f9: cylinder r=9.14mm len=12.7mm, axis (0,1,0), area 11.4mm2, adj f10,f12,f19,f25
  f10: plane 18.32x17.69mm, normal (0,-1,0), area 144.3mm2, adj f1,f2,f3,f4,f5,f6,f7,f8
  f11: cylinder r=9.14mm len=12.7mm, axis (0,1,0), area 11.4mm2, adj f10,f12,f14,f20
  f12: plane 18.32x17.69mm, normal (0,1,0), area 153.5mm2, adj f0,f1,f2,f3,f4,f5,f6,f7
  f13: cylinder r=5.71mm len=12.7mm, axis (0,1,0), area 6.2mm2, adj f10,f12,f16,f17
  f14: extruded ~12.7x2.91mm, area 39.3mm2, adj f10,f11,f12,f16
  f15: extruded ~12.7x2.23mm, area 39.3mm2, adj f1,f10,f12,f17
  f16: cylinder r=0.63mm len=12.7mm, axis (0,1,0), area 11.7mm2, adj f10,f12,f13,f14
  f17: cylinder r=0.63mm len=12.7mm, axis (0,1,0), area 11.7mm2, adj f10,f12,f13,f15
  f18: cylinder r=5.71mm len=12.7mm, axis (0,1,0), area 6.2mm2, adj f10,f12,f21,f22
  f19: extruded ~12.7x2.23mm, area 39.3mm2, adj f9,f10,f12,f21
  f20: extruded ~12.7x2.91mm, area 39.3mm2, adj f10,f11,f12,f22
  f21: cylinder r=0.63mm len=12.7mm, axis (0,1,0), area 11.7mm2, adj f10,f12,f18,f19
  f22: cylinder r=0.63mm len=12.7mm, axis (0,1,0), area 11.7mm2, adj f10,f12,f18,f20
  f23: cylinder r=5.71mm len=12.7mm, axis (0,1,0), area 6.2mm2, adj f10,f12,f26,f27
  f24: extruded ~12.7x2.97mm, area 39.3mm2, adj f8,f10,f12,f26
  f25: extruded ~12.7x2.73mm, area 39.3mm2, adj f9,f10,f12,f27
  f26: cylinder r=0.63mm len=12.7mm, axis (0,1,0), area 11.7mm2, adj f10,f12,f23,f24
  f27: cylinder r=0.63mm len=12.7mm, axis (0,1,0), area 11.7mm2, adj f10,f12,f23,f25
  f28: cylinder r=5.71mm len=12.7mm, axis (0,1,0), area 6.2mm2, adj f10,f12,f31,f32
  f29: extruded ~12.7x2.58mm, area 39.3mm2, adj f7,f10,f12,f31
  f30: extruded ~12.7x2.58mm, area 39.3mm2, adj f8,f10,f12,f32
  f31: cylinder r=0.63mm len=12.7mm, axis (0,1,0), area 11.7mm2, adj f10,f12,f28,f29
  f32: cylinder r=0.63mm len=12.7mm, axis (0,1,0), area 11.7mm2, adj f10,f12,f28,f30
  f33: cylinder r=5.71mm len=12.7mm, axis (0,1,0), area 6.2mm2, adj f10,f12,f36,f37
  f34: extruded ~12.7x2.91mm, area 39.3mm2, adj f6,f10,f12,f36
  f35: extruded ~12.7x2.23mm, area 39.3mm2, adj f5,f10,f12,f37
  f36: cylinder r=0.63mm len=12.7mm, axis (0,1,0), area 11.7mm2, adj f10,f12,f33,f34
  f37: cylinder r=0.63mm len=12.7mm, axis (0,1,0), area 11.7mm2, adj f10,f12,f33,f35
  f38: cylinder r=5.71mm len=12.7mm, axis (0,1,0), area 6.2mm2, adj f10,f12,f41,f42
  f39: extruded ~12.7x2.73mm, area 39.3mm2, adj f5,f10,f12,f41
  f40: extruded ~12.7x2.97mm, area 39.3mm2, adj f7,f10,f12,f42
  f41: cylinder r=0.63mm len=12.7mm, axis (0,1,0), area 11.7mm2, adj f10,f12,f38,f39
  f42: cylinder r=0.63mm len=12.7mm, axis (0,1,0), area 11.7mm2, adj f10,f12,f38,f40
  f43: cylinder r=5.71mm len=12.7mm, axis (0,1,0), area 6.2mm2, adj f10,f12,f46,f47
  f44: extruded ~12.7x2.97mm, area 39.3mm2, adj f4,f10,f12,f46
  f45: extruded ~12.7x2.73mm, area 39.3mm2, adj f3,f10,f12,f47
  f46: cylinder r=0.63mm len=12.7mm, axis (0,1,0), area 11.7mm2, adj f10,f12,f43,f44
  f47: cylinder r=0.63mm len=12.7mm, axis (0,1,0), area 11.7mm2, adj f10,f12,f43,f45
  f48: cylinder r=5.71mm len=12.7mm, axis (0,1,0), area 6.2mm2, adj f10,f12,f51,f52
  f49: extruded ~12.7x2.23mm, area 39.3mm2, adj f3,f10,f12,f51
  f50: extruded ~12.7x2.91mm, area 39.3mm2, adj f6,f10,f12,f52
  f51: cylinder r=0.63mm len=12.7mm, axis (0,1,0), area 11.7mm2, adj f10,f12,f48,f49
  f52: cylinder r=0.63mm len=12.7mm, axis (0,1,0), area 11.7mm2, adj f10,f12,f48,f50
  f53: cylinder r=5.71mm len=12.7mm, axis (0,1,0), area 6.2mm2, adj f10,f12,f56,f57
  f54: extruded ~12.7x2.58mm, area 39.3mm2, adj f2,f10,f12,f56
  f55: extruded ~12.7x2.58mm, area 39.3mm2, adj f4,f10,f12,f57
  f56: cylinder r=0.63mm len=12.7mm, axis (0,1,0), area 11.7mm2, adj f10,f12,f53,f54
  f57: cylinder r=0.63mm len=12.7mm, axis (0,1,0), area 11.7mm2, adj f10,f12,f53,f55
  f58: cylinder r=5.71mm len=12.7mm, axis (0,1,0), area 6.2mm2, adj f10,f12,f61,f62
  f59: extruded ~12.7x2.73mm, area 39.3mm2, adj f1,f10,f12,f61
  f60: extruded ~12.7x2.97mm, area 39.3mm2, adj f2,f10,f12,f62
  f61: cylinder r=0.63mm len=12.7mm, axis (0,1,0), area 11.7mm2, adj f10,f12,f58,f59
  f62: cylinder r=0.63mm len=12.7mm, axis (0,1,0), area 11.7mm2, adj f10,f12,f58,f60
  f63: plane 6.2x6.2mm, normal (0,-1,0), area 9.2mm2, adj f0,f64
  f64: cylinder r=3.1mm len=6.2mm, axis (0,-1,0), area 48.7mm2, adj f10,f63
PLACE A at identity fixed
PLACE B t=(0,-6.35,0)mm
MATE fastened B.f1 <-> A.f1  axis (0,1,0) through (0,-6.35,0)mm
